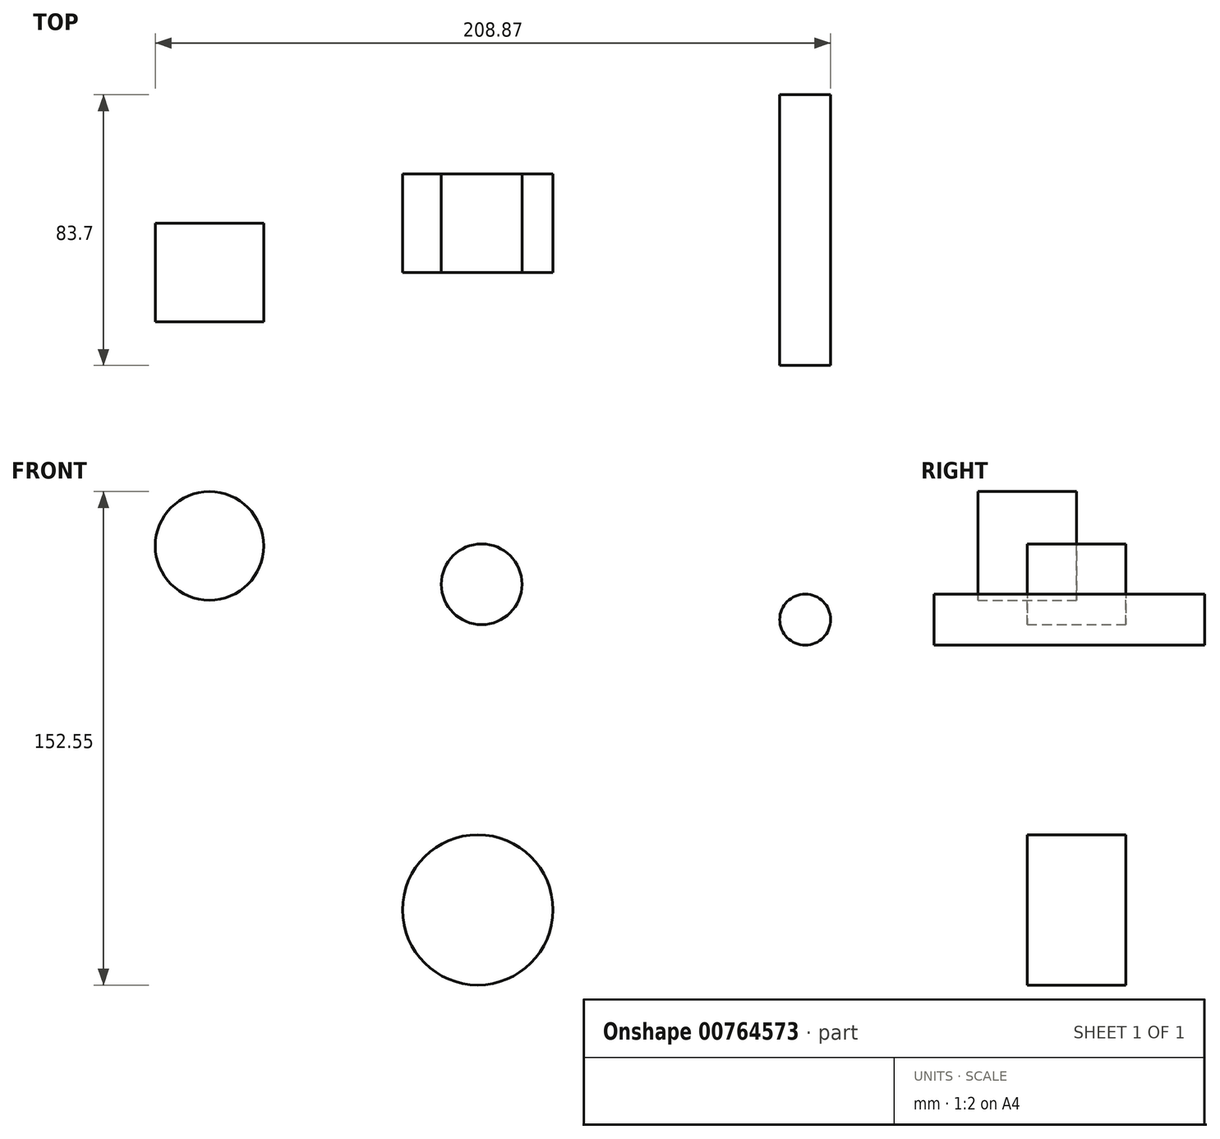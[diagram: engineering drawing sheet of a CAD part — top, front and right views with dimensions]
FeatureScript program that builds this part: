
annotation { "Feature Type Name" : "Feature", "Feature Type Description" : "" }
export const myFeature = defineFeature(function(context is Context, id is Id, definition is map)
    precondition{}
    {
        {
            var Q0;
            Q0=qCreatedBy(makeId("Front.planeOp"),FACE);
            var sketch = newSketch(context, id + "F0", { "sketchPlane" : qUnion([Q0])});
            skCircle(sketch, "E0", {"center": v(-56.68, 51.17) * mm, "radius": 12.47 * mm});
            skCircle(sketch, "E1", {"center": v(43.36, 40.23) * mm, "radius": 7.88 * mm});
            skSolve(sketch);
        }
        {
            var Q0;
            Q0=makeQuery(id+"F0.imprint","IMPRINT",FACE,{"disambiguationData":[TD([[makeQuery(id+"F0.imprint","IMPRINT",EDGE,{"derivedFrom":sQuery(id+"F0.wireOp",EDGE,"E0")}),1.0]])]});
            extrude(context, id + "F1", {"entities" : qUnion([Q0]), "endBound" : BoundingType.SYMMETRIC, "depth" : 30.48 * mm, "offsetDistance" : 30.48 * mm});
        }
        {
            var Q0;
            Q0=qCreatedBy(makeId("Top.planeOp"),FACE);
            var sketch = newSketch(context, id + "F2", { "sketchPlane" : qUnion([Q0])});
            skLineSegment(sketch, "E2", {"start": v(-15.16, -44) * mm, "end": v(-15.16, 39.7) * mm});
            skSolve(sketch);
        }
        {
            var Q0;
            Q0=makeQuery(id+"F0.imprint","IMPRINT",FACE,{"disambiguationData":[TD([[makeQuery(id+"F0.imprint","IMPRINT",EDGE,{"derivedFrom":sQuery(id+"F0.wireOp",EDGE,"E1")}),1.0]])]});
            var Q1;
            Q1=sQuery(id+"F2.wireOp",EDGE,"E2");
            sweep(context, id + "F3", {"profiles" : qUnion([Q0]), "path" : qUnion([Q1])});
        }
        {
            var Q0;
            Q0=qCreatedBy(makeId("Front.planeOp"),FACE);
            var sketch = newSketch(context, id + "F4", { "sketchPlane" : qUnion([Q0])});
            skCircle(sketch, "E3", {"center": v(-140.85, 63.02) * mm, "radius": 16.78 * mm});
            skSolve(sketch);
        }
        {
            var Q0;
            Q0 = qSketchRegion(id + "F4", true);
            extrude(context, id + "F5", {"entities" : qUnion([Q0]), "depth" : 30.48 * mm, "offsetDistance" : 30.48 * mm});
        }
        {
            var Q0;
            Q0=qCreatedBy(makeId("Front.planeOp"),FACE);
            var sketch = newSketch(context, id + "F6", { "sketchPlane" : qUnion([Q0])});
            skCircle(sketch, "E4", {"center": v(-57.89, -49.52) * mm, "radius": 23.23 * mm});
            skSolve(sketch);
        }
        {
            var Q0;
            Q0 = qSketchRegion(id + "F6", true);
            extrude(context, id + "F7", {"entities" : qUnion([Q0]), "endBound" : BoundingType.SYMMETRIC, "depth" : 30.48 * mm, "offsetDistance" : 30.48 * mm});
        }
    });
